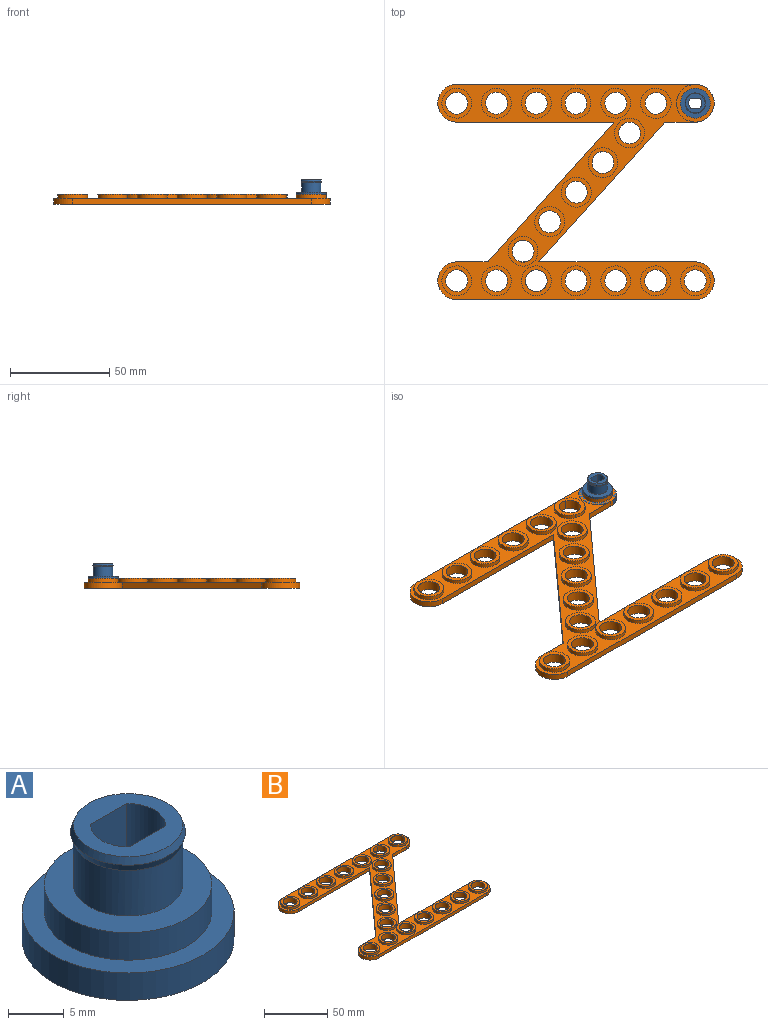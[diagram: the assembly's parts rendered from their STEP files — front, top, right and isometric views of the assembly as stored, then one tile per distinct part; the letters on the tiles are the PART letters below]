
ASSEMBLY  parts=2 mates=1
PART A: 13 faces, bbox 19x19x12.5 mm
  f0: cylinder r=3.35mm len=12.5mm, axis (0,0,-1), area 68.7mm2, adj f1,f4,f6,f10
  f1: plane 12.5x4.57mm, normal (0,1,0), area 57.1mm2, adj f0,f2,f6,f10
  f2: cylinder r=3.35mm len=12.5mm, axis (0,0,-1), area 68.7mm2, adj f1,f4,f6,f10
  f3: cylinder r=9.5mm len=19mm, axis (0,0,-1), area 179.1mm2, adj f5,f6
  f4: plane 12.5x4.57mm, normal (0,-1,0), area 57.1mm2, adj f0,f2,f6,f10
  f5: plane 19x19mm, normal (0,0,1), area 106.8mm2, adj f3,f7
  f6: plane 19x19mm, normal (0,0,-1), area 253.9mm2, adj f0,f1,f2,f3,f4
  f7: cylinder r=7.5mm len=15mm, axis (0,0,-1), area 141.4mm2, adj f5,f8
  f8: plane 15x15mm, normal (0,0,1), area 101.3mm2, adj f7,f9
  f9: cylinder r=4.9mm len=9.8mm, axis (0,0,-1), area 153.9mm2, adj f8,f11
  f10: plane 9.8x9.8mm, normal (0,0,1), area 45.8mm2, adj f0,f1,f2,f4,f12
  f11: cone r=5.15mm half-angle=18.4deg, axis (0,0,1), area 25mm2, adj f9,f12
  f12: cone r=4.9mm half-angle=18.4deg, axis (0,0,-1), area 25mm2, adj f10,f11
PART B: 77 faces, bbox 139x108.3x5 mm
  f0: plane 78.66x3mm, normal (0,1,0), area 236mm2, adj f4,f14,f15,f74
  f1: plane 15.77x3mm, normal (0,1,0), area 47.3mm2, adj f6,f14,f15,f73
  f2: cylinder r=5.5mm len=11mm, axis (0,0,-1), area 165.3mm2, adj f15,f21,f75,f76
  f3: plane 2.47x0.14mm, normal (0,0,1), area 0.2mm2, adj f5,f67
  f4: cylinder r=9.5mm len=19mm, axis (0,0,-1), area 89.5mm2, adj f0,f12,f14,f15
  f5: plane 3x2.47mm, normal (0,1,0), area 7.4mm2, adj f3,f15,f67
  f6: cylinder r=9.5mm len=19mm, axis (0,0,-1), area 89.5mm2, adj f1,f12,f14,f15
  f7: cylinder r=5.5mm len=11mm, axis (0,0,-1), area 172.8mm2, adj f15,f27
  f8: cylinder r=5.5mm len=11mm, axis (0,0,-1), area 172.8mm2, adj f15,f25
  f9: cylinder r=5.5mm len=11mm, axis (0,0,-1), area 172.8mm2, adj f15,f23
  f10: cylinder r=5.5mm len=11mm, axis (0,0,-1), area 172.8mm2, adj f15,f19
  f11: cylinder r=5.5mm len=11mm, axis (0,0,-1), area 172.8mm2, adj f15,f17
  f12: plane 120x3mm, normal (0,-1,0), area 360mm2, adj f4,f6,f14,f15
  f13: cylinder r=5.5mm len=11mm, axis (0,0,-1), area 172.8mm2, adj f15,f29
  f14: plane 139x108.3mm, normal (0,0,1), area 3562mm2, adj f0,f1,f4,f6,f12,f16,f18,f20
  f15: plane 139x108.3mm, normal (0,0,-1), area 5123.4mm2, adj f0,f1,f2,f4,f5,f6,f7,f8
  f16: cylinder r=7.5mm len=15mm, axis (0,0,-1), area 94.2mm2, adj f14,f17
  f17: plane 15x15mm, normal (0,0,1), area 81.7mm2, adj f11,f16
  f18: cylinder r=7.5mm len=15mm, axis (0,0,-1), area 94.2mm2, adj f14,f19
  f19: plane 15x15mm, normal (0,0,1), area 81.7mm2, adj f10,f18
  f20: cylinder r=7.5mm len=15mm, axis (0,0,-1), area 94.2mm2, adj f14,f21
  f21: plane 15x15mm, normal (0,0,1), area 81.7mm2, adj f2,f20
  f22: cylinder r=7.5mm len=15mm, axis (0,0,-1), area 94.2mm2, adj f14,f23
  f23: plane 15x15mm, normal (0,0,1), area 81.7mm2, adj f9,f22
  f24: cylinder r=7.5mm len=15mm, axis (0,0,-1), area 94.2mm2, adj f14,f25
  f25: plane 15x15mm, normal (0,0,1), area 81.7mm2, adj f8,f24
  f26: cylinder r=7.5mm len=15mm, axis (0,0,-1), area 94.2mm2, adj f14,f27
  f27: plane 15x15mm, normal (0,0,1), area 81.7mm2, adj f7,f26
  f28: cylinder r=7.5mm len=15mm, axis (0,0,-1), area 94.2mm2, adj f14,f29
  f29: plane 15x15mm, normal (0,0,1), area 81.7mm2, adj f13,f28
  f30: plane 15x15mm, normal (0,0,1), area 81.7mm2, adj f31,f42
  f31: cylinder r=7.5mm len=15mm, axis (0,0,-1), area 94.2mm2, adj f14,f30
  f32: plane 15x15mm, normal (0,0,1), area 81.7mm2, adj f33,f48
  f33: cylinder r=7.5mm len=15mm, axis (0,0,-1), area 94.2mm2, adj f14,f32
  f34: plane 15x15mm, normal (0,0,1), area 81.7mm2, adj f35,f47
  f35: cylinder r=7.5mm len=15mm, axis (0,0,-1), area 94.2mm2, adj f14,f34
  f36: plane 15x15mm, normal (0,0,1), area 81.7mm2, adj f37,f46
  f37: cylinder r=7.5mm len=15mm, axis (0,0,-1), area 94.2mm2, adj f14,f36
  f38: plane 15x15mm, normal (0,0,1), area 81.7mm2, adj f39,f45
  f39: cylinder r=7.5mm len=15mm, axis (0,0,-1), area 94.2mm2, adj f14,f38
  f40: plane 15x15mm, normal (0,0,1), area 81.7mm2, adj f41,f44
  f41: cylinder r=7.5mm len=15mm, axis (0,0,-1), area 94.2mm2, adj f14,f40
  f42: cylinder r=5.5mm len=11mm, axis (0,0,-1), area 172.8mm2, adj f15,f30
  f43: plane 79.1x3mm, normal (0,-1,0), area 237.3mm2, adj f14,f15,f49,f73
  f44: cylinder r=5.5mm len=11mm, axis (0,0,-1), area 172.8mm2, adj f15,f40
  f45: cylinder r=5.5mm len=11mm, axis (0,0,-1), area 172.8mm2, adj f15,f38
  f46: cylinder r=5.5mm len=11mm, axis (0,0,-1), area 172.8mm2, adj f15,f36
  f47: cylinder r=5.5mm len=11mm, axis (0,0,-1), area 172.8mm2, adj f15,f34
  f48: cylinder r=5.5mm len=11mm, axis (0,0,-1), area 172.8mm2, adj f15,f32
  f49: cylinder r=9.5mm len=19mm, axis (0,0,-1), area 89.5mm2, adj f14,f15,f43,f50
  f50: plane 120x3mm, normal (0,1,0), area 360mm2, adj f14,f15,f49,f51
  f51: cylinder r=9.5mm len=19mm, axis (0,0,-1), area 89.5mm2, adj f14,f15,f50,f52
  f52: plane 15.33x3mm, normal (0,-1,0), area 46mm2, adj f14,f15,f51,f74
  f53: cylinder r=5.5mm len=10.45mm, axis (0,0,-1), area 84.7mm2, adj f15,f55,f66
  f54: cylinder r=7.5mm len=14.42mm, axis (0,0,-1), area 47.8mm2, adj f14,f55,f72
  f55: plane 15.32x15.14mm, normal (0,0,1), area 90.6mm2, adj f53,f54,f66,f72
  f56: plane 15x15mm, normal (0,0,1), area 81.7mm2, adj f57,f71
  f57: cylinder r=7.5mm len=15mm, axis (0,0,-1), area 94.2mm2, adj f14,f56
  f58: plane 15x15mm, normal (0,0,1), area 81.7mm2, adj f59,f70
  f59: cylinder r=7.5mm len=15mm, axis (0,0,-1), area 94.2mm2, adj f14,f58
  f60: plane 15x15mm, normal (0,0,1), area 81.7mm2, adj f61,f69
  f61: cylinder r=7.5mm len=15mm, axis (0,0,-1), area 94.2mm2, adj f14,f60
  f62: plane 15x15mm, normal (0,0,1), area 81.7mm2, adj f63,f68
  f63: cylinder r=7.5mm len=15mm, axis (0,0,-1), area 94.2mm2, adj f14,f62
  f64: plane 15x15mm, normal (0,0,1), area 81.7mm2, adj f65,f67
  f65: cylinder r=7.5mm len=15mm, axis (0,0,-1), area 94.2mm2, adj f14,f64
  f66: cylinder r=5.5mm len=10.45mm, axis (0,0,-1), area 84.7mm2, adj f15,f53,f55
  f67: cylinder r=5.5mm len=11mm, axis (0,0,-1), area 165.3mm2, adj f3,f5,f15,f64
  f68: cylinder r=5.5mm len=11mm, axis (0,0,-1), area 172.8mm2, adj f15,f62
  f69: cylinder r=5.5mm len=11mm, axis (0,0,-1), area 172.8mm2, adj f15,f60
  f70: cylinder r=5.5mm len=11mm, axis (0,0,-1), area 172.8mm2, adj f15,f58
  f71: cylinder r=5.5mm len=11mm, axis (0,0,-1), area 172.8mm2, adj f15,f56
  f72: cylinder r=7.5mm len=14.42mm, axis (0,0,-1), area 47.8mm2, adj f14,f54,f55
  f73: plane 70.3x63.33mm, normal (-0.74,0.67,0), area 283.8mm2, adj f1,f14,f15,f43
  f74: plane 70.3x63.33mm, normal (0.74,-0.67,0), area 283.8mm2, adj f0,f14,f15,f52
  f75: plane 1.83x1.65mm, normal (0,0,1), area 0.2mm2, adj f2,f76
  f76: plane 3x1.83mm, normal (0.74,-0.67,0), area 7.4mm2, adj f2,f15,f75
PLACE A rot(axis=(0,0,1),0deg) t=(120,89.3,0)mm
PLACE B at identity fixed
MATE fastened B.f31 <-> A.f0  axis (0,0,-1) through (120,89.3,0)mm
